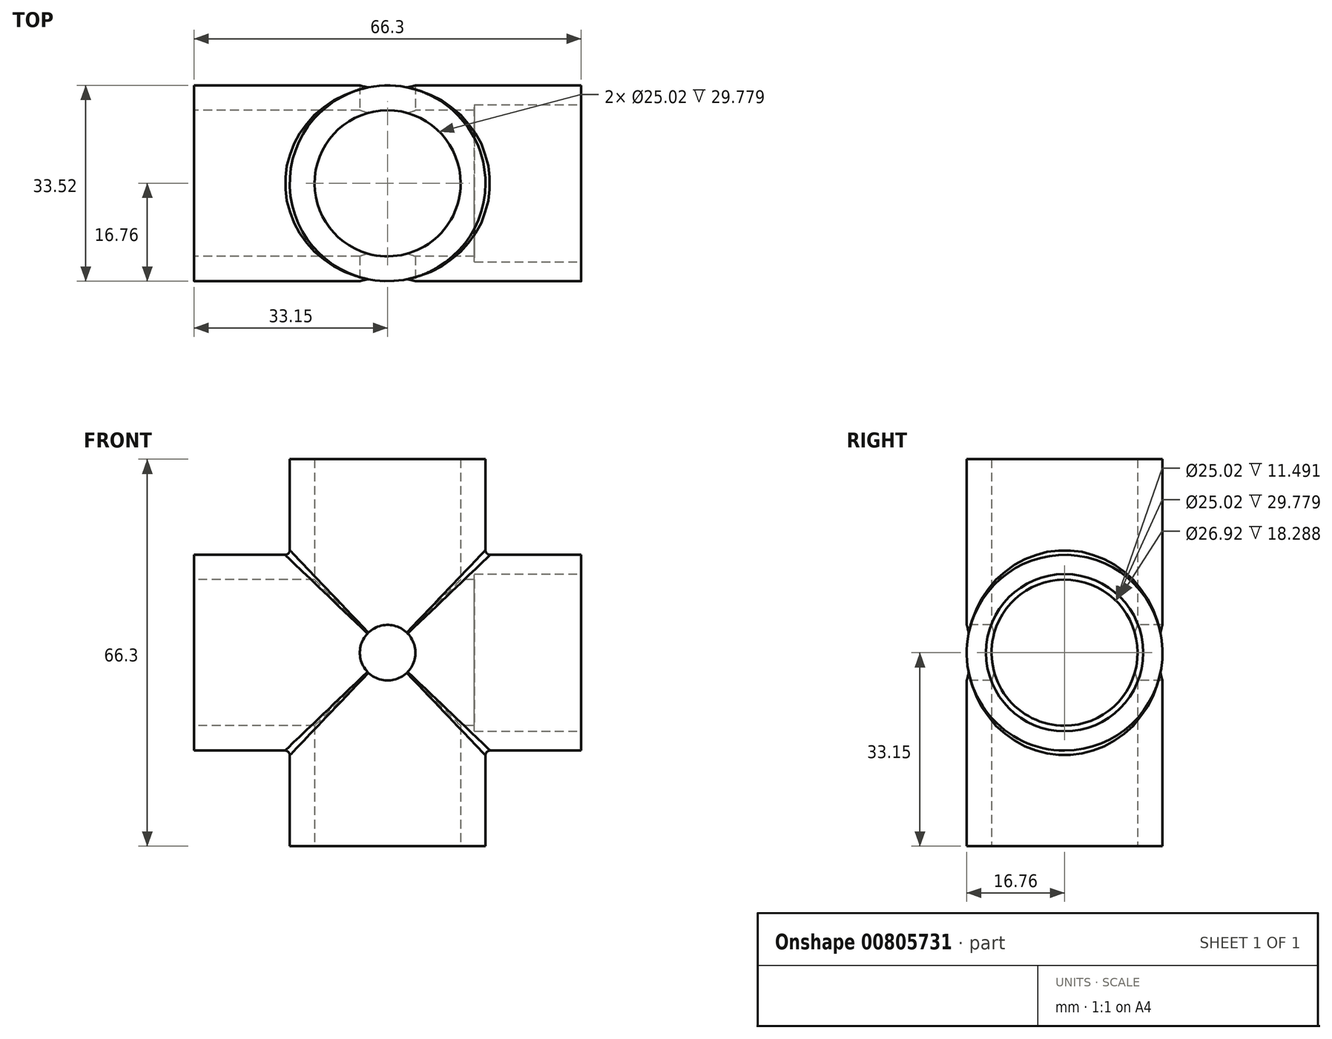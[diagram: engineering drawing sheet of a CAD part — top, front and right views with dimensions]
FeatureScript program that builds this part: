
annotation { "Feature Type Name" : "Feature", "Feature Type Description" : "" }
export const myFeature = defineFeature(function(context is Context, id is Id, definition is map)
    precondition{}
    {
        {
            var Q0;
            Q0=qCreatedBy(makeId("Right.planeOp"),FACE);
            var sketch = newSketch(context, id + "F0", { "sketchPlane" : qUnion([Q0])});
            skCircle(sketch, "E0", {"center": v(0, 0) * mm, "radius": 16.76 * mm});
            skCircle(sketch, "E1", {"center": v(0, 0) * mm, "radius": 12.5 * mm});
            skSolve(sketch);
        }
        {
            var Q0;
            Q0 = qSketchRegion(id + "F0", true);
            extrude(context, id + "F1", {"entities" : qUnion([Q0]), "depth" : 66.3 * mm, "offsetDistance" : 25.4 * mm, "symmetric" : true});
        }
        {
            var Q0;
            Q0=qCreatedBy(makeId("Top.planeOp"),FACE);
            var sketch = newSketch(context, id + "F2", { "sketchPlane" : qUnion([Q0])});
            skCircle(sketch, "E2", {"center": v(0, 0) * mm, "radius": 16.76 * mm});
            skCircle(sketch, "E3", {"center": v(0, 0) * mm, "radius": 12.5 * mm});
            skSolve(sketch);
        }
        {
            var Q0;
            Q0=makeQuery(id+"F2.imprint","IMPRINT",FACE,{"disambiguationData":[TD([[makeQuery(id+"F2.imprint","IMPRINT",EDGE,{"derivedFrom":sQuery(id+"F2.wireOp",EDGE,"E2")}),1.0]])]});
            var Q1;
            Q1=sQuery(id+"F2.wireOp",EDGE,"E2");
            var Q2;
            Q2=sQuery(id+"F2.wireOp",EDGE,"E3");
            extrude(context, id + "F3", {"entities" : qUnion([Q0]), "operationType" : NewBodyOperationType.ADD, "surfaceEntities" : qUnion([Q1, Q2]), "depth" : 66.3 * mm, "offsetDistance" : 25.4 * mm, "symmetric" : true});
        }
        {
            var Q0;
            Q0=makeQuery(id+"F0.imprint","IMPRINT",FACE,{"disambiguationData":[TD([[makeQuery(id+"F0.imprint","IMPRINT",EDGE,{"derivedFrom":sQuery(id+"F0.wireOp",EDGE,"E1")}),1.0]])]});
            extrude(context, id + "F4", {"entities" : qUnion([Q0]), "operationType" : NewBodyOperationType.REMOVE, "endBound" : BoundingType.THROUGH_ALL, "oppositeDirection" : true, "depth" : 25.4 * mm, "offsetDistance" : 25.4 * mm, "hasSecondDirection" : true, "secondDirectionBound" : BoundingType.THROUGH_ALL, "secondDirectionOppositeDirection" : false, "secondDirectionDepth" : 25.4 * mm});
        }
        {
            var Q0;
            Q0=makeQuery(id+"F2.imprint","IMPRINT",FACE,{"disambiguationData":[TD([[makeQuery(id+"F2.imprint","IMPRINT",EDGE,{"derivedFrom":sQuery(id+"F2.wireOp",EDGE,"E3")}),1.0]])]});
            extrude(context, id + "F5", {"entities" : qUnion([Q0]), "operationType" : NewBodyOperationType.REMOVE, "endBound" : BoundingType.THROUGH_ALL, "oppositeDirection" : true, "depth" : 25.4 * mm, "offsetDistance" : 25.4 * mm, "hasSecondDirection" : true, "secondDirectionBound" : BoundingType.THROUGH_ALL, "secondDirectionOppositeDirection" : false, "secondDirectionDepth" : 25.4 * mm});
        }
        {
            var Q0;
            Q0=qCreatedBy(makeId("Top.planeOp"),FACE);
            var sketch = newSketch(context, id + "F6", { "sketchPlane" : qUnion([Q0])});
            skLineSegment(sketch, "E4", {"start": v(0, 0.98) * mm, "end": v(0, -34.37) * mm});
            skSolve(sketch);
        }
        {
            var Q0;
            Q0=makeQuery(id+"F1.opExtrude","CAP_FACE",FACE,{"disambiguationData":[OSD([sQuery(id+"F0.wireOp",EDGE,"E0"),sQuery(id+"F0.wireOp",EDGE,"E1")])],"isStart":false});
            var sketch = newSketch(context, id + "F7", { "sketchPlane" : qUnion([Q0])});
            skCircle(sketch, "E5", {"center": v(0, 0) * mm, "radius": 13.46 * mm});
            skSolve(sketch);
        }
        {
            var Q0;
            Q0 = qSketchRegion(id + "F7", true);
            extrude(context, id + "F8", {"entities" : qUnion([Q0]), "operationType" : NewBodyOperationType.REMOVE, "oppositeDirection" : true, "depth" : 18.29 * mm, "offsetDistance" : 25.4 * mm});
        }
        {
            var Q0;
            Q0=makeQuery(id+"F3.boolean.opBoolean","INTERSECT",EDGE,{"disambiguationData":[OD(3.0)],"derivedFrom":[makeQuery(id+"F1.opExtrude","SWEPT_FACE",FACE,{"disambiguationData":[OSD([sQuery(id+"F0.wireOp",EDGE,"E0")])]}),makeQuery(id+"F3.opExtrude","SWEPT_FACE",FACE,{"disambiguationData":[OSD([sQuery(id+"F2.wireOp",EDGE,"E2")])]})]});
            var Q1;
            Q1=makeQuery(id+"F3.boolean.opBoolean","INTERSECT",EDGE,{"disambiguationData":[OD(1.0)],"derivedFrom":[makeQuery(id+"F1.opExtrude","SWEPT_FACE",FACE,{"disambiguationData":[OSD([sQuery(id+"F0.wireOp",EDGE,"E0")])]}),makeQuery(id+"F3.opExtrude","SWEPT_FACE",FACE,{"disambiguationData":[OSD([sQuery(id+"F2.wireOp",EDGE,"E2")])]})]});
            var Q2;
            Q2=makeQuery(id+"F3.boolean.opBoolean","INTERSECT",EDGE,{"disambiguationData":[OD(0.0)],"derivedFrom":[makeQuery(id+"F1.opExtrude","SWEPT_FACE",FACE,{"disambiguationData":[OSD([sQuery(id+"F0.wireOp",EDGE,"E0")])]}),makeQuery(id+"F3.opExtrude","SWEPT_FACE",FACE,{"disambiguationData":[OSD([sQuery(id+"F2.wireOp",EDGE,"E2")])]})]});
            var Q3;
            Q3=makeQuery(id+"F3.boolean.opBoolean","INTERSECT",EDGE,{"disambiguationData":[OD(2.0)],"derivedFrom":[makeQuery(id+"F1.opExtrude","SWEPT_FACE",FACE,{"disambiguationData":[OSD([sQuery(id+"F0.wireOp",EDGE,"E0")])]}),makeQuery(id+"F3.opExtrude","SWEPT_FACE",FACE,{"disambiguationData":[OSD([sQuery(id+"F2.wireOp",EDGE,"E2")])]})]});
            fillet(context, id + "F9", {"entities" : qUnion([Q0, Q1, Q2, Q3]), "radius" : 0.81 * mm, "tangentPropagation" : true, "allowEdgeOverflow" : false});
        }
        {
            var Q0;
            Q0=qCreatedBy(makeId("Front.planeOp"),FACE);
            var sketch = newSketch(context, id + "F10", { "sketchPlane" : qUnion([Q0])});
            skCircle(sketch, "E6", {"center": v(0, 0) * mm, "radius": 4.76 * mm});
            skSolve(sketch);
        }
        {
            var Q0;
            Q0 = qSketchRegion(id + "F10", true);
            extrude(context, id + "F11", {"entities" : qUnion([Q0]), "operationType" : NewBodyOperationType.REMOVE, "endBound" : BoundingType.THROUGH_ALL, "oppositeDirection" : true, "depth" : 25.4 * mm, "offsetDistance" : 25.4 * mm, "hasSecondDirection" : true, "secondDirectionBound" : BoundingType.THROUGH_ALL, "secondDirectionOppositeDirection" : false, "secondDirectionDepth" : 25.4 * mm});
        }
    });
